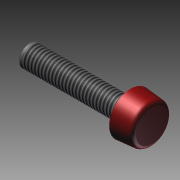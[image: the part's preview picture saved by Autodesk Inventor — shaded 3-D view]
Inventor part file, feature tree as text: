
AUTODESK INVENTOR PART (.ipt)
format: ipt  version: 2011 SP1 (Build 150282100, 282)  size: 101,376 bytes
history: native  units: mm
features: other x7, revolve x1, thread x1, sketch x1
ambient origin geometry x8: Origin, YZ Plane, XZ Plane, XY Plane, X Axis, Y Axis, Z Axis, Center Point
bodies: Solid1 (feature_tree)
feature tree (10):
  revolve  "Revolution1"  [1 undecoded]
  thread  "Thread1"  [1 undecoded]
  other  "AS_XY"
  other  "AS_YZ"
  other  "AS_ZX"
  other  "AS_X"
  other  "AS_Y"
  other  "AS_Z"
  other  "AS_Center"
  sketch  "Skizze_1"  dims[d0=360.0deg d1=23.5mm d2=0.5mm]
note: 2 required parameter values undecoded (feature->parameter linkage not recoverable at this tier; creation-order binding heuristic only, values carry confidence <= 0.55)